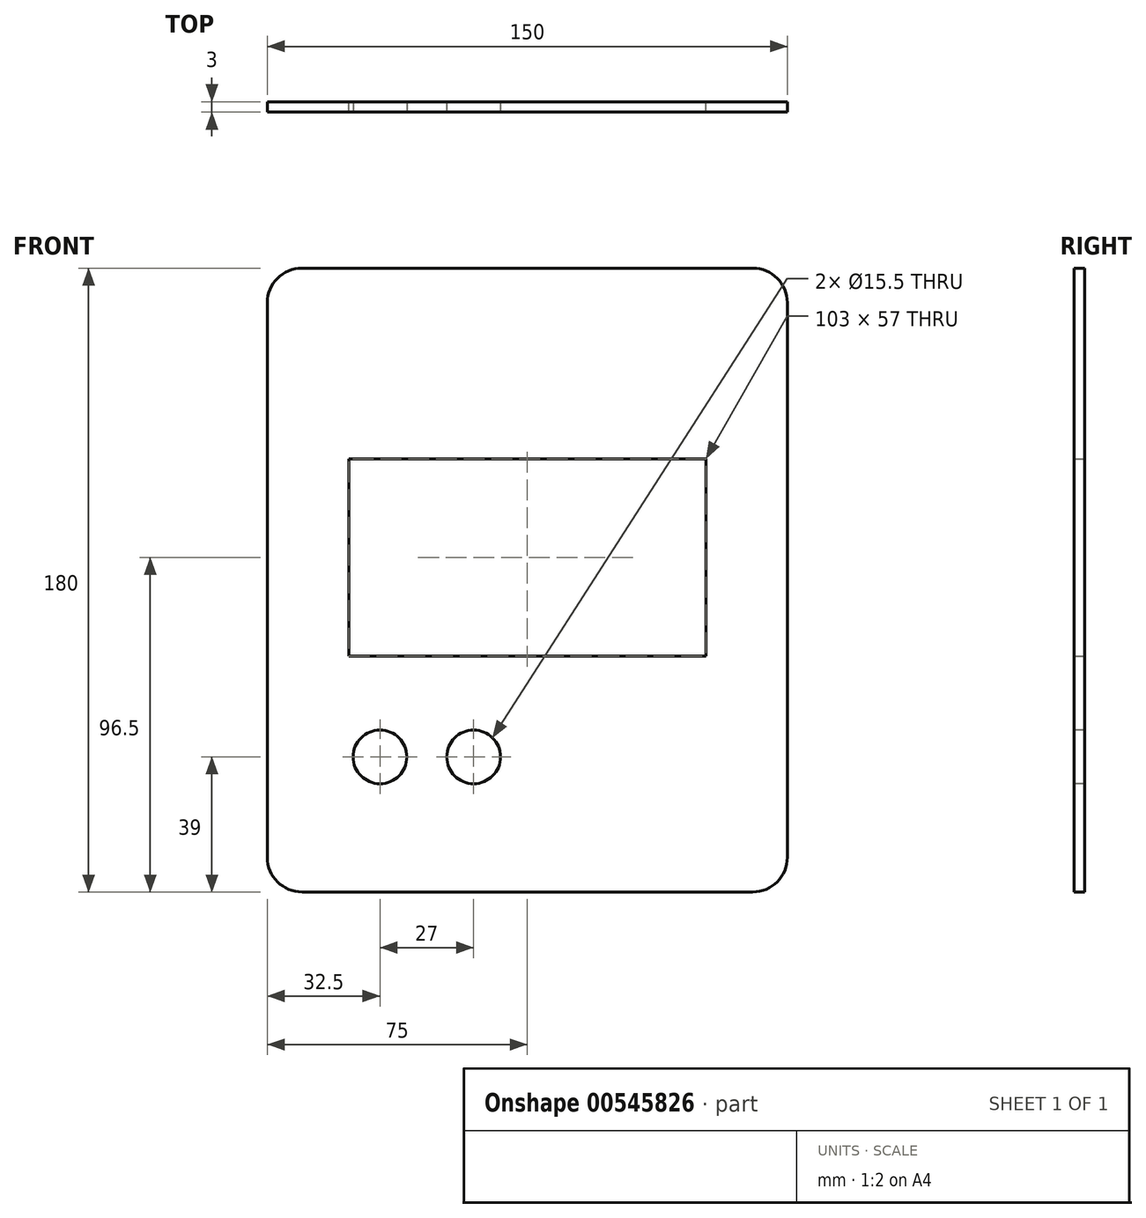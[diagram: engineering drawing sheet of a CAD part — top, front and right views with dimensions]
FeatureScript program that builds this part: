
annotation { "Feature Type Name" : "Feature", "Feature Type Description" : "" }
export const myFeature = defineFeature(function(context is Context, id is Id, definition is map)
    precondition{}
    {
        {
            var Q0;
            Q0=qCreatedBy(makeId("Front.planeOp"),FACE);
            var sketch = newSketch(context, id + "F0", { "sketchPlane" : qUnion([Q0])});
            skLineSegment(sketch, "E0.bottom", {"start": v(10, 0) * mm, "end": v(140, 0) * mm});
            skLineSegment(sketch, "E0.top", {"start": v(10, 180) * mm, "end": v(140, 180) * mm});
            skLineSegment(sketch, "E0.left", {"start": v(0, 10) * mm, "end": v(0, 170) * mm});
            skLineSegment(sketch, "E0.right", {"start": v(150, 10) * mm, "end": v(150, 170) * mm});
            skPoint(sketch, "E1.visualSharp", {"position": v(0, 180) * mm});
            skArc(sketch, "E1.filletArc", {"start": v(10, 180) * mm, "mid": v(2.93, 177.07) * mm, "end": v(0, 170) * mm});
            skPoint(sketch, "E2.visualSharp", {"position": v(150, 180) * mm});
            skArc(sketch, "E2.filletArc", {"start": v(150, 170) * mm, "mid": v(147.07, 177.07) * mm, "end": v(140, 180) * mm});
            skPoint(sketch, "E3.visualSharp", {"position": v(150, 0) * mm});
            skArc(sketch, "E3.filletArc", {"start": v(140, 0) * mm, "mid": v(147.07, 2.93) * mm, "end": v(150, 10) * mm});
            skPoint(sketch, "E4.visualSharp", {"position": v(0, 0) * mm});
            skArc(sketch, "E4.filletArc", {"start": v(0, 10) * mm, "mid": v(2.93, 2.93) * mm, "end": v(10, 0) * mm});
            skSolve(sketch);
        }
        {
            var Q0;
            Q0=makeQuery(id+"F0.imprint","IMPRINT",FACE,{"disambiguationData":[TD([[makeQuery(id+"F0.imprint","IMPRINT",EDGE,{"derivedFrom":sQuery(id+"F0.wireOp",EDGE,"E0.bottom")}),1.0]])]});
            extrude(context, id + "F1", {"entities" : qUnion([Q0]), "depth" : 3 * mm, "offsetDistance" : 25 * mm});
        }
        {
            var Q0;
            Q0=makeQuery(id+"F0.imprint","IMPRINT",FACE,{"disambiguationData":[TD([[makeQuery(id+"F0.imprint","IMPRINT",EDGE,{"derivedFrom":sQuery(id+"F0.wireOp",EDGE,"E0.bottom")}),1.0]])]});
            var sketch = newSketch(context, id + "F2", { "sketchPlane" : qUnion([Q0])});
            skLineSegment(sketch, "E5.bottom", {"start": v(23.5, 125) * mm, "end": v(126.5, 125) * mm});
            skLineSegment(sketch, "E5.top", {"start": v(23.5, 68) * mm, "end": v(126.5, 68) * mm});
            skLineSegment(sketch, "E5.left", {"start": v(23.5, 125) * mm, "end": v(23.5, 68) * mm});
            skLineSegment(sketch, "E5.right", {"start": v(126.5, 125) * mm, "end": v(126.5, 68) * mm});
            skLineSegment(sketch, "E6", {"start": v(75, 166.96) * mm, "end": v(75, 59.24) * mm, "construction": true});
            skSolve(sketch);
        }
        {
            var Q0;
            Q0 = qSketchRegion(id + "F2", true);
            var Q1;
            Q1=makeQuery(id+"F1.opExtrude","CAP_FACE",FACE,{"disambiguationData":[OSD([sQuery(id+"F0.wireOp",EDGE,"E0.bottom"),sQuery(id+"F0.wireOp",EDGE,"E0.top"),sQuery(id+"F0.wireOp",EDGE,"E0.left"),sQuery(id+"F0.wireOp",EDGE,"E0.right"),sQuery(id+"F0.wireOp",EDGE,"E1.filletArc"),sQuery(id+"F0.wireOp",EDGE,"E2.filletArc"),sQuery(id+"F0.wireOp",EDGE,"E3.filletArc"),sQuery(id+"F0.wireOp",EDGE,"E4.filletArc")])],"isStart":false});
            extrude(context, id + "F3", {"entities" : qUnion([Q0, Q1]), "operationType" : NewBodyOperationType.REMOVE, "endBound" : BoundingType.THROUGH_ALL, "depth" : 25 * mm, "offsetDistance" : 25 * mm});
        }
        {
            var Q0;
            Q0=makeQuery(id+"F1.opExtrude","CAP_FACE",FACE,{"disambiguationData":[OSD([sQuery(id+"F0.wireOp",EDGE,"E0.bottom"),sQuery(id+"F0.wireOp",EDGE,"E0.top"),sQuery(id+"F0.wireOp",EDGE,"E0.left"),sQuery(id+"F0.wireOp",EDGE,"E0.right"),sQuery(id+"F0.wireOp",EDGE,"E1.filletArc"),sQuery(id+"F0.wireOp",EDGE,"E2.filletArc"),sQuery(id+"F0.wireOp",EDGE,"E3.filletArc"),sQuery(id+"F0.wireOp",EDGE,"E4.filletArc")])],"isStart":false});
            var sketch = newSketch(context, id + "F4", { "sketchPlane" : qUnion([Q0])});
            skLineSegment(sketch, "E7.bottom", {"start": v(23.5, 48) * mm, "end": v(41.5, 48) * mm, "construction": true});
            skLineSegment(sketch, "E7.top", {"start": v(23.5, 30) * mm, "end": v(41.5, 30) * mm, "construction": true});
            skLineSegment(sketch, "E7.left", {"start": v(23.5, 48) * mm, "end": v(23.5, 30) * mm, "construction": true});
            skLineSegment(sketch, "E7.right", {"start": v(41.5, 48) * mm, "end": v(41.5, 30) * mm, "construction": true});
            skLineSegment(sketch, "E8.bottom", {"start": v(50.5, 48) * mm, "end": v(68.5, 48) * mm, "construction": true});
            skLineSegment(sketch, "E8.top", {"start": v(50.5, 30) * mm, "end": v(68.5, 30) * mm, "construction": true});
            skLineSegment(sketch, "E8.left", {"start": v(50.5, 48) * mm, "end": v(50.5, 30) * mm, "construction": true});
            skLineSegment(sketch, "E8.right", {"start": v(68.5, 48) * mm, "end": v(68.5, 30) * mm, "construction": true});
            skCircle(sketch, "E9", {"center": v(32.5, 39) * mm, "radius": 7.75 * mm});
            skCircle(sketch, "E10", {"center": v(59.5, 39) * mm, "radius": 7.75 * mm});
            skPoint(sketch, "E11", {"position": v(50.5, 39) * mm});
            skPoint(sketch, "E12", {"position": v(32.5, 30) * mm});
            skPoint(sketch, "E13", {"position": v(41.5, 39) * mm});
            skLineSegment(sketch, "E14", {"start": v(23.5, 30) * mm, "end": v(41.5, 48) * mm, "construction": true});
            skLineSegment(sketch, "E15", {"start": v(23.5, 48) * mm, "end": v(41.5, 30) * mm, "construction": true});
            skLineSegment(sketch, "E16", {"start": v(50.5, 48) * mm, "end": v(68.5, 30) * mm, "construction": true});
            skLineSegment(sketch, "E17", {"start": v(68.5, 48) * mm, "end": v(50.5, 30) * mm, "construction": true});
            skSolve(sketch);
        }
        {
            var Q0;
            Q0 = qSketchRegion(id + "F4", true);
            extrude(context, id + "F5", {"entities" : qUnion([Q0]), "operationType" : NewBodyOperationType.REMOVE, "oppositeDirection" : true, "depth" : 25 * mm, "offsetDistance" : 25 * mm});
        }
    });
